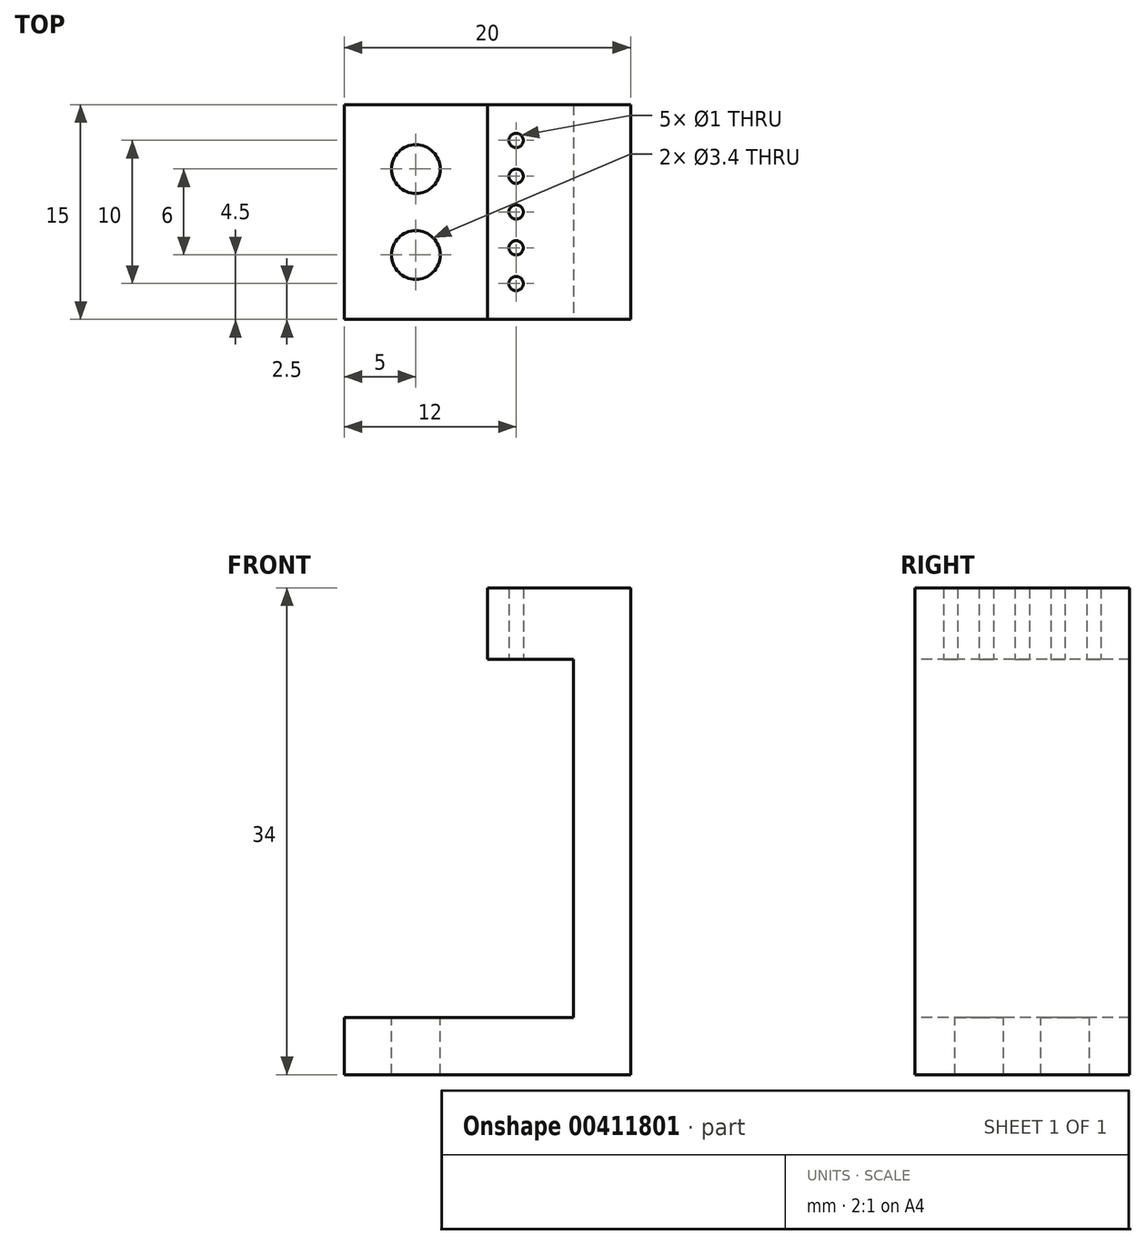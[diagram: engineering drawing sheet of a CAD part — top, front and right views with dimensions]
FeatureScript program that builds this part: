
annotation { "Feature Type Name" : "Feature", "Feature Type Description" : "" }
export const myFeature = defineFeature(function(context is Context, id is Id, definition is map)
    precondition{}
    {
        {
            var Q0;
            Q0=qCreatedBy(makeId("Top.planeOp"),FACE);
            var sketch = newSketch(context, id + "F0", { "sketchPlane" : qUnion([Q0])});
            skLineSegment(sketch, "E0.bottom", {"start": v(0, 7.5) * mm, "end": v(-20, 7.5) * mm});
            skLineSegment(sketch, "E0.top", {"start": v(0, -7.5) * mm, "end": v(-20, -7.5) * mm});
            skLineSegment(sketch, "E0.left", {"start": v(0, 7.5) * mm, "end": v(0, -7.5) * mm});
            skLineSegment(sketch, "E0.right", {"start": v(-20, 7.5) * mm, "end": v(-20, -7.5) * mm});
            skLineSegment(sketch, "E1", {"start": v(-4, 7.5) * mm, "end": v(-4, -7.5) * mm});
            skCircle(sketch, "E2", {"center": v(-15, 3) * mm, "radius": 1.7 * mm});
            skCircle(sketch, "E3", {"center": v(-15, -3) * mm, "radius": 1.7 * mm});
            skSolve(sketch);
        }
        {
            var Q0;
            {var subQ0=sQuery(id+"F0.wireOp",EDGE,"E0.right");Q0=makeQuery(id+"F0.imprint","IMPRINT",FACE,{"disambiguationData":[TD([[makeQuery(id+"F0.imprint","IMPRINT",EDGE,{"derivedFrom":subQ0}),1.0]])]});}
            var Q1;
            {var subQ0=sQuery(id+"F0.wireOp",EDGE,"E0.left");Q1=makeQuery(id+"F0.imprint","IMPRINT",FACE,{"disambiguationData":[TD([[makeQuery(id+"F0.imprint","IMPRINT",EDGE,{"derivedFrom":subQ0}),-1.0]])]});}
            extrude(context, id + "F1", {"entities" : qUnion([Q0, Q1]), "oppositeDirection" : true, "depth" : 4 * mm, "offsetDistance" : 25 * mm});
        }
        {
            var Q0;
            {var subQ0=sQuery(id+"F0.wireOp",EDGE,"E0.left");Q0=makeQuery(id+"F0.imprint","IMPRINT",FACE,{"disambiguationData":[TD([[makeQuery(id+"F0.imprint","IMPRINT",EDGE,{"derivedFrom":subQ0}),-1.0]])]});}
            extrude(context, id + "F2", {"entities" : qUnion([Q0]), "operationType" : NewBodyOperationType.ADD, "depth" : 25 * mm, "offsetDistance" : 25 * mm});
        }
        {
            var Q0;
            Q0=makeQuery(id+"F2.opExtrude","CAP_FACE",FACE,{"disambiguationData":[OSD([sQuery(id+"F0.wireOp",EDGE,"E0.bottom"),sQuery(id+"F0.wireOp",EDGE,"E0.top"),sQuery(id+"F0.wireOp",EDGE,"E0.left"),sQuery(id+"F0.wireOp",EDGE,"E1")])],"isStart":false});
            var sketch = newSketch(context, id + "F3", { "sketchPlane" : qUnion([Q0])});
            skPoint(sketch, "E4.oppositeSnap0", {"position": v(-2, -7.5) * mm});
            skLineSegment(sketch, "E4.bottom", {"start": v(0, 7.5) * mm, "end": v(-10, 7.5) * mm});
            skLineSegment(sketch, "E4.top", {"start": v(0, -7.5) * mm, "end": v(-10, -7.5) * mm});
            skLineSegment(sketch, "E4.left", {"start": v(0, 7.5) * mm, "end": v(0, -7.5) * mm});
            skLineSegment(sketch, "E4.right", {"start": v(-10, 7.5) * mm, "end": v(-10, -7.5) * mm});
            skCircle(sketch, "E5", {"center": v(-8, 5) * mm, "radius": 0.5 * mm});
            skCircle(sketch, "E6", {"center": v(-8, 2.5) * mm, "radius": 0.5 * mm});
            skCircle(sketch, "E7", {"center": v(-8, 0) * mm, "radius": 0.5 * mm});
            skCircle(sketch, "E8", {"center": v(-8, -2.5) * mm, "radius": 0.5 * mm});
            skCircle(sketch, "E9", {"center": v(-8, -5) * mm, "radius": 0.5 * mm});
            skSolve(sketch);
        }
        {
            var Q0;
            {var subQ0=sQuery(id+"F3.wireOp",EDGE,"E4.right");Q0=makeQuery(id+"F3.imprint","IMPRINT",FACE,{"disambiguationData":[TD([[makeQuery(id+"F3.imprint","IMPRINT",EDGE,{"derivedFrom":subQ0}),1.0]])]});}
            var Q1;
            {var subQ0=sQuery(id+"F3.wireOp",EDGE,"E4.left");Q1=makeQuery(id+"F3.imprint","IMPRINT",FACE,{"disambiguationData":[TD([[makeQuery(id+"F3.imprint","IMPRINT",EDGE,{"derivedFrom":subQ0}),-1.0]])]});}
            extrude(context, id + "F4", {"entities" : qUnion([Q0, Q1]), "operationType" : NewBodyOperationType.ADD, "depth" : 5 * mm, "offsetDistance" : 25 * mm});
        }
    });
